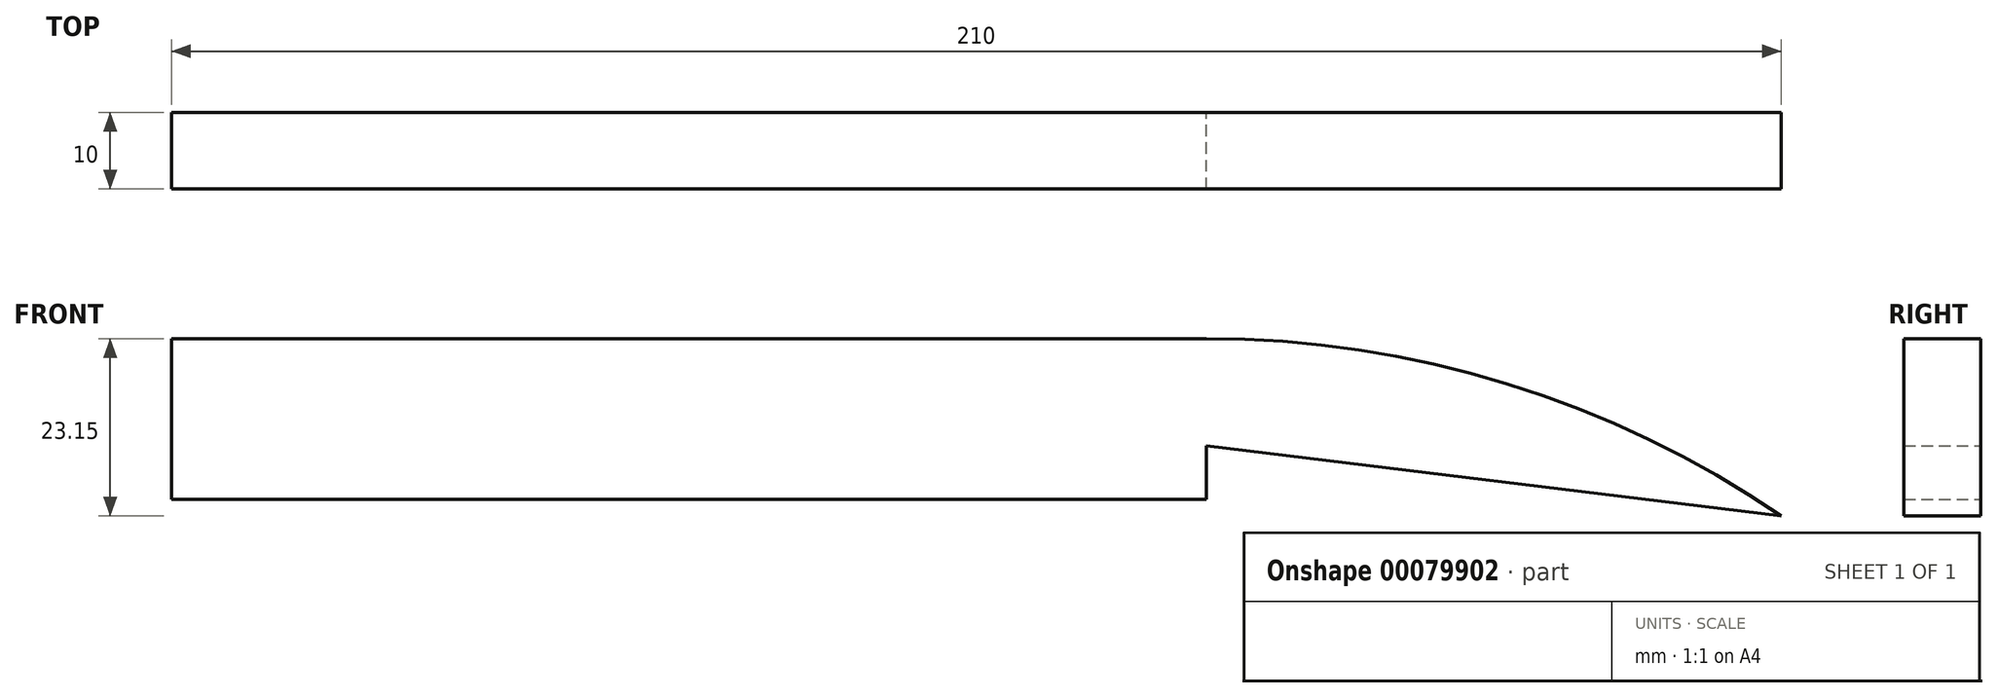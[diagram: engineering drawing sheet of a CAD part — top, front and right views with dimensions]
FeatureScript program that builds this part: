
annotation { "Feature Type Name" : "Feature", "Feature Type Description" : "" }
export const myFeature = defineFeature(function(context is Context, id is Id, definition is map)
    precondition{}
    {
        {
            var Q0;
            Q0=qCreatedBy(makeId("Front.planeOp"),FACE);
            var sketch = newSketch(context, id + "F0", { "sketchPlane" : qUnion([Q0])});
            skLineSegment(sketch, "E0.bottom", {"start": v(0, -8) * mm, "end": v(135, -8) * mm});
            skLineSegment(sketch, "E0.top", {"start": v(0, -29) * mm, "end": v(135, -29) * mm});
            skLineSegment(sketch, "E0.left", {"start": v(0, -8) * mm, "end": v(0, -29) * mm});
            skLineSegment(sketch, "E1", {"start": v(135, -29) * mm, "end": v(135, -22) * mm});
            skLineSegment(sketch, "E2", {"start": v(135, -22) * mm, "end": v(210, -31.15) * mm});
            skArc(sketch, "E3", {"start": v(210, -31.15) * mm, "mid": v(174.25, -13.92) * mm, "end": v(135, -8) * mm});
            skSolve(sketch);
        }
        {
            var Q0;
            Q0=makeQuery(id+"F0.imprint","IMPRINT",FACE,{"disambiguationData":[TD([[makeQuery(id+"F0.imprint","IMPRINT",EDGE,{"derivedFrom":sQuery(id+"F0.wireOp",EDGE,"E0.bottom")}),-1.0]])]});
            extrude(context, id + "F1", {"entities" : qUnion([Q0]), "depth" : 10 * mm});
        }
    });
